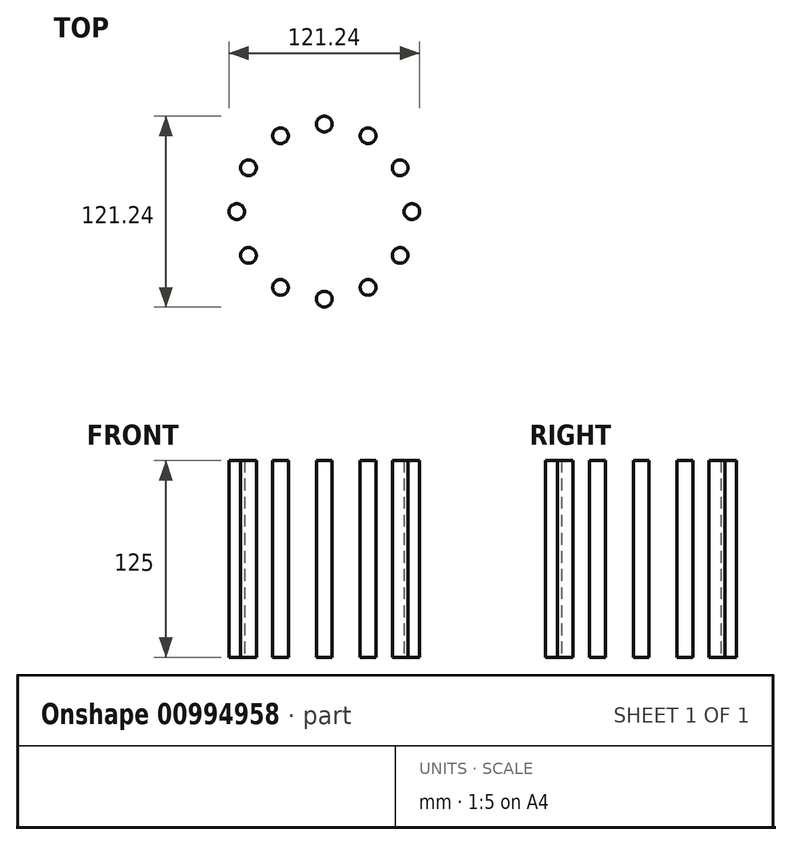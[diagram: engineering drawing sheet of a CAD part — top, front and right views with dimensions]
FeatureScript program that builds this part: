
annotation { "Feature Type Name" : "Feature", "Feature Type Description" : "" }
export const myFeature = defineFeature(function(context is Context, id is Id, definition is map)
    precondition{}
    {
        {
            var Q0;
            Q0=qCreatedBy(makeId("Top.planeOp"),FACE);
            var sketch = newSketch(context, id + "F0", { "sketchPlane" : qUnion([Q0])});
            skCircle(sketch, "E0", {"center": v(-55.62, 0) * mm, "radius": 5 * mm});
            skSolve(sketch);
        }
        {
            var Q0;
            Q0=makeQuery(id+"F0.imprint","IMPRINT",FACE,{"disambiguationData":[TD([[makeQuery(id+"F0.imprint","IMPRINT",EDGE,{"derivedFrom":sQuery(id+"F0.wireOp",EDGE,"E0")}),1.0]])]});
            extrude(context, id + "F1", {"entities" : qUnion([Q0]), "endBound" : BoundingType.SYMMETRIC, "depth" : 125 * mm, "offsetDistance" : 25 * mm});
        }
        {
            var Q0;
            Q0=qCreatedBy(makeId("Front.planeOp"),FACE);
            var sketch = newSketch(context, id + "F2", { "sketchPlane" : qUnion([Q0])});
            skLineSegment(sketch, "E1", {"start": v(0, 0) * mm, "end": v(0, 43.02) * mm, "construction": true});
            skSolve(sketch);
        }
        {
            var Q0;
            Q0=makeQuery(id+"F1.opExtrude","SWEPT_BODY",BODY,{"disambiguationData":[OSD([sQuery(id+"F0.wireOp",EDGE,"E0")])]});
            var Q1;
            Q1=sQuery(id+"F2.wireOp",EDGE,"E1");
            circularPattern(context, id + "F3", {"entities" : qUnion([Q0]), "axis" : qUnion([Q1]), "angle" : 360 * degree, "instanceCount" : 12, "equalSpace" : true});
        }
    });
